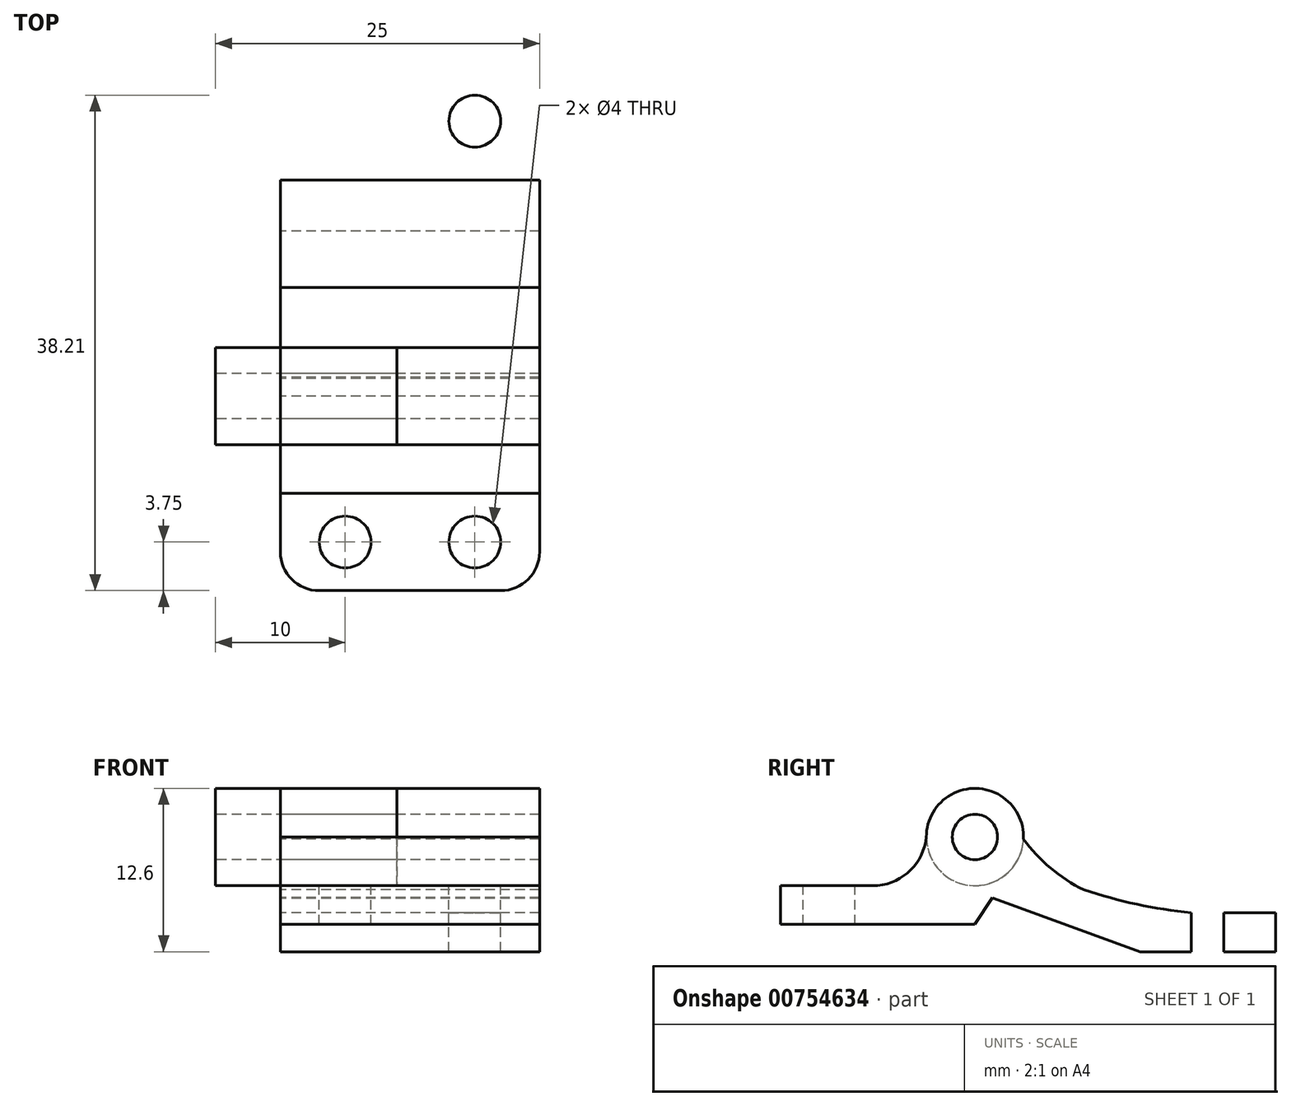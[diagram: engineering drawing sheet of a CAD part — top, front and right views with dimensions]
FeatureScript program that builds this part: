
annotation { "Feature Type Name" : "Feature", "Feature Type Description" : "" }
export const myFeature = defineFeature(function(context is Context, id is Id, definition is map)
    precondition{}
    {
        {
            var Q0;
            Q0=qCreatedBy(makeId("Right.planeOp"),FACE);
            var sketch = newSketch(context, id + "F0", { "sketchPlane" : qUnion([Q0])});
            skArc(sketch, "E0", {"start": v(2.7, 4.14) * mm, "mid": v(1.4, 10.23) * mm, "end": v(-3.75, 6.75) * mm});
            skCircle(sketch, "E1", {"center": v(0, 6.75) * mm, "radius": 1.75 * mm});
            skPoint(sketch, "E2", {"position": v(-3.75, 6.75) * mm});
            skPoint(sketch, "E3", {"position": v(-3.75, 3) * mm});
            skPoint(sketch, "E4", {"position": v(-7.5, 3) * mm});
            skArc(sketch, "E5", {"start": v(-7.5, 3) * mm, "mid": v(-4.95, 4.2) * mm, "end": v(-3.75, 6.75) * mm});
            skPoint(sketch, "E6", {"position": v(0, 3) * mm});
            skPoint(sketch, "E7", {"position": v(3.75, 6.75) * mm});
            skPoint(sketch, "E8", {"position": v(2.7, 4.14) * mm});
            skLineSegment(sketch, "E9", {"start": v(2.7, 4.14) * mm, "end": v(0, 0) * mm});
            skPoint(sketch, "E10", {"position": v(-15, 3) * mm});
            skPoint(sketch, "E11", {"position": v(-15, 0) * mm});
            skLineSegment(sketch, "E12", {"start": v(-7.5, 3) * mm, "end": v(-15, 3) * mm});
            skLineSegment(sketch, "E13", {"start": v(-15, 3) * mm, "end": v(-15, 0) * mm});
            skLineSegment(sketch, "E14", {"start": v(-15, 0) * mm, "end": v(0, 0) * mm});
            skSolve(sketch);
        }
        {
            var Q0;
            Q0=makeQuery(id+"F0.imprint","IMPRINT",FACE,{"disambiguationData":[TD([[makeQuery(id+"F0.imprint","IMPRINT",EDGE,{"derivedFrom":sQuery(id+"F0.wireOp",EDGE,"E0")}),1.0]])]});
            extrude(context, id + "F1", {"entities" : qUnion([Q0]), "depth" : 20 * mm, "offsetDistance" : 25 * mm});
        }
        {
            var Q0;
            Q0=makeQuery(id+"F1.opExtrude","SWEPT_FACE",FACE,{"disambiguationData":[OSD([sQuery(id+"F0.wireOp",EDGE,"E12")])]});
            var sketch = newSketch(context, id + "F2", { "sketchPlane" : qUnion([Q0])});
            skLineSegment(sketch, "E15", {"start": v(10, -7.5) * mm, "end": v(10, -15) * mm, "construction": true});
            skPoint(sketch, "E16", {"position": v(10, -11.25) * mm});
            skLineSegment(sketch, "E17", {"start": v(10, -11.25) * mm, "end": v(20, -11.25) * mm, "construction": true});
            skLineSegment(sketch, "E18", {"start": v(10, -11.25) * mm, "end": v(0, -11.25) * mm, "construction": true});
            skPoint(sketch, "E19", {"position": v(5, -11.25) * mm});
            skPoint(sketch, "E20", {"position": v(15, -11.25) * mm});
            skCircle(sketch, "E21", {"center": v(5, -11.25) * mm, "radius": 2 * mm});
            skCircle(sketch, "E22", {"center": v(15, -11.25) * mm, "radius": 2 * mm});
            skSolve(sketch);
        }
        {
            var Q0;
            Q0=makeQuery(id+"F2.imprint","IMPRINT",FACE,{"disambiguationData":[TD([[makeQuery(id+"F2.imprint","IMPRINT",EDGE,{"derivedFrom":sQuery(id+"F2.wireOp",EDGE,"E21")}),1.0]])]});
            var Q1;
            Q1=makeQuery(id+"F2.imprint","IMPRINT",FACE,{"disambiguationData":[TD([[makeQuery(id+"F2.imprint","IMPRINT",EDGE,{"derivedFrom":sQuery(id+"F2.wireOp",EDGE,"E22")}),1.0]])]});
            var Q2;
            Q2=makeQuery(id+"F1.opExtrude","SWEPT_FACE",FACE,{"disambiguationData":[OSD([sQuery(id+"F0.wireOp",EDGE,"E14")])]});
            extrude(context, id + "F3", {"entities" : qUnion([Q0, Q1]), "operationType" : NewBodyOperationType.REMOVE, "endBound" : BoundingType.UP_TO_SURFACE, "oppositeDirection" : true, "depth" : 25 * mm, "endBoundEntityFace" : qUnion([Q2]), "offsetDistance" : 25 * mm});
        }
        {
            var Q0;
            Q0=makeQuery(id+"F1.opExtrude","CAP_EDGE",EDGE,{"disambiguationData":[OSD([sQuery(id+"F0.wireOp",EDGE,"E13")])],"isStart":true});
            var Q1;
            Q1=makeQuery(id+"F1.opExtrude","CAP_EDGE",EDGE,{"disambiguationData":[OSD([sQuery(id+"F0.wireOp",EDGE,"E13")])],"isStart":false});
            fillet(context, id + "F4", {"entities" : qUnion([Q0, Q1]), "radius" : 3 * mm, "tangentPropagation" : true, "allowEdgeOverflow" : false});
        }
        {
            var Q0;
            Q0=qCreatedBy(makeId("Right.planeOp"),FACE);
            var sketch = newSketch(context, id + "F5", { "sketchPlane" : qUnion([Q0])});
            skCircle(sketch, "E23", {"center": v(0, 6.75) * mm, "radius": 1.75 * mm});
            skCircle(sketch, "E24", {"center": v(0, 6.75) * mm, "radius": 3.75 * mm});
            skPoint(sketch, "E25", {"position": v(1.46, 2) * mm});
            skLineSegment(sketch, "E26", {"start": v(1.46, 2) * mm, "end": v(12.74, -2.1) * mm});
            skLineSegment(sketch, "E27", {"start": v(12.74, -2.1) * mm, "end": v(34.74, -2.1) * mm});
            skLineSegment(sketch, "E28", {"start": v(0, 6.75) * mm, "end": v(14.1, 1.62) * mm, "construction": true});
            skLineSegment(sketch, "E29", {"start": v(14.1, 1.62) * mm, "end": v(12.74, -2.1) * mm, "construction": true});
            skLineSegment(sketch, "E30", {"start": v(1.46, 2) * mm, "end": v(0, 3) * mm});
            skLineSegment(sketch, "E31", {"start": v(34.74, -2.1) * mm, "end": v(34.74, 0.9) * mm});
            skLineSegment(sketch, "E32", {"start": v(34.74, 0.9) * mm, "end": v(16.68, 0.9) * mm});
            skArc(sketch, "E33", {"start": v(3.75, 6.58) * mm, "mid": v(5.84, 4.35) * mm, "end": v(8.4, 2.67) * mm});
            skArc(sketch, "E34", {"start": v(8.4, 2.67) * mm, "mid": v(12.5, 1.56) * mm, "end": v(16.68, 0.9) * mm});
            skPoint(sketch, "E35.orphan", {"position": v(13.83, 0.9) * mm});
            skPoint(sketch, "E36.end.orphan", {"position": v(2.96, 4.44) * mm});
            skSolve(sketch);
        }
        {
            var Q0;
            Q0=makeQuery(id+"F5.imprint","IMPRINT",FACE,{"disambiguationData":[TD([[makeQuery(id+"F5.imprint","IMPRINT",EDGE,{"derivedFrom":sQuery(id+"F5.wireOp",EDGE,"E23")}),-1.0]])]});
            extrude(context, id + "F6", {"entities" : qUnion([Q0]), "oppositeDirection" : true, "depth" : 5 * mm, "offsetDistance" : 25 * mm});
        }
        {
            var Q0;
            Q0=makeQuery(id+"F5.imprint","IMPRINT",FACE,{"disambiguationData":[TD([[makeQuery(id+"F5.imprint","IMPRINT",EDGE,{"derivedFrom":sQuery(id+"F5.wireOp",EDGE,"E26")}),1.0]])]});
            var Q1;
            Q1=makeQuery(id+"F5.imprint","IMPRINT",FACE,{"disambiguationData":[TD([[makeQuery(id+"F5.imprint","IMPRINT",EDGE,{"derivedFrom":sQuery(id+"F5.wireOp",EDGE,"E23")}),-1.0]])]});
            extrude(context, id + "F7", {"entities" : qUnion([Q0, Q1]), "operationType" : NewBodyOperationType.ADD, "depth" : 20 * mm, "offsetDistance" : 25 * mm});
        }
        {
            var Q0;
            Q0=makeQuery(id+"F7.opExtrude","CAP_EDGE",EDGE,{"disambiguationData":[OSD([sQuery(id+"F5.wireOp",EDGE,"E31")])],"isStart":false});
            var Q1;
            Q1=makeQuery(id+"F7.opExtrude","CAP_EDGE",EDGE,{"disambiguationData":[OSD([sQuery(id+"F5.wireOp",EDGE,"E31")])],"isStart":true});
            fillet(context, id + "F8", {"entities" : qUnion([Q0, Q1]), "radius" : 3 * mm, "tangentPropagation" : true, "allowEdgeOverflow" : false});
        }
        {
            var Q0;
            Q0=makeQuery(id+"F7.opExtrude","SWEPT_FACE",FACE,{"disambiguationData":[OSD([sQuery(id+"F5.wireOp",EDGE,"E32")])]});
            var sketch = newSketch(context, id + "F9", { "sketchPlane" : qUnion([Q0])});
            skLineSegment(sketch, "E37", {"start": v(10, 16.68) * mm, "end": v(10, 34.74) * mm, "construction": true});
            skLineSegment(sketch, "E38", {"start": v(20, 24.2) * mm, "end": v(0, 24.2) * mm, "construction": true});
            skCircle(sketch, "E39", {"center": v(10, 30.24) * mm, "radius": 2 * mm});
            skCircle(sketch, "E40", {"center": v(5, 21.2) * mm, "radius": 2 * mm});
            skCircle(sketch, "E41.MirrorC", {"center": v(15, 21.2) * mm, "radius": 2 * mm});
            skSolve(sketch);
        }
        {
            var Q0;
            Q0=makeQuery(id+"F9.imprint","IMPRINT",FACE,{"disambiguationData":[TD([[makeQuery(id+"F9.imprint","IMPRINT",EDGE,{"derivedFrom":sQuery(id+"F9.wireOp",EDGE,"E39")}),1.0]])]});
            var Q1;
            Q1=makeQuery(id+"F9.imprint","IMPRINT",FACE,{"disambiguationData":[TD([[makeQuery(id+"F9.imprint","IMPRINT",EDGE,{"derivedFrom":sQuery(id+"F9.wireOp",EDGE,"E40")}),1.0]])]});
            var Q2;
            Q2=makeQuery(id+"F9.imprint","IMPRINT",FACE,{"disambiguationData":[TD([[makeQuery(id+"F9.imprint","IMPRINT",EDGE,{"derivedFrom":sQuery(id+"F9.wireOp",EDGE,"E41.MirrorC")}),-1.0]])]});
            var Q3;
            Q3=makeQuery(id+"F7.opExtrude","SWEPT_FACE",FACE,{"disambiguationData":[OSD([sQuery(id+"F5.wireOp",EDGE,"E27")])]});
            extrude(context, id + "F10", {"entities" : qUnion([Q0, Q1, Q2]), "operationType" : NewBodyOperationType.REMOVE, "endBound" : BoundingType.UP_TO_SURFACE, "oppositeDirection" : true, "depth" : 25 * mm, "endBoundEntityFace" : qUnion([Q3]), "offsetDistance" : 25 * mm});
        }
        {
            var Q0;
            Q0=qCreatedBy(makeId("Right.planeOp"),FACE);
            var sketch = newSketch(context, id + "F11", { "sketchPlane" : qUnion([Q0])});
            skCircle(sketch, "E42", {"center": v(0, 6.75) * mm, "radius": 1.75 * mm});
            skCircle(sketch, "E43", {"center": v(0, 6.75) * mm, "radius": 3.75 * mm});
            skSolve(sketch);
        }
        {
            var Q0;
            Q0=makeQuery(id+"F11.imprint","IMPRINT",FACE,{"disambiguationData":[TD([[makeQuery(id+"F11.imprint","IMPRINT",EDGE,{"derivedFrom":sQuery(id+"F11.wireOp",EDGE,"E42")}),-1.0]])]});
            extrude(context, id + "F12", {"entities" : qUnion([Q0]), "depth" : 9 * mm, "offsetDistance" : 25 * mm});
        }
    });
